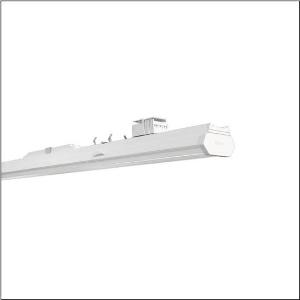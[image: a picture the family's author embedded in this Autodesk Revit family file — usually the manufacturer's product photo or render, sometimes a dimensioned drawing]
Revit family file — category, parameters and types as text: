
# Revit family: licross_r__11_protected_mo_51tp12dn495g3c_6ec9
name_source: partatom
category: Lighting Fixtures
units: mm (PartAtom-declared; Revit-internal decimal feet)

## family parameters
Cut with Voids When Loaded = No
Host = Face
Light Source = No
Part Type = Normal
Room Calculation Point = No
Round Connector Dimension = Use Diameter
Shared = No

## types (1)
- --- (1 x LED, 980 lm, 6.8 W, 4000K)
    Apparent Load = 7 VA
    CIE Flux Codes = 73 92 98 99 100
    Color Rendering = 80
    Color Temperature = 4000K
    Default Elevation = 1800 mm
    Description = Licross® 11 Protected MO, luminaire insert, of sheet steel, galvanised, coil coated, white, length: 1.500mm, width: 90mm, height: 101mm, LED rated luminous flux: 9.980lm, light colour: 840, control gear: DALI 2 (for two DALI lines), with plug, 6-pole, with phase selection, for trunking rail, 14-core, mains connection: 220..240V, AC, 50/60Hz, rated input power: 61W, for trunking rail, 14-core, halogen-free wiring, for emergency light function, converter,control gear: single battery element, battery: LiFePO4, 9Ah, primary light control with lens, of plastic, primary optical cover: cover, of PMMA, light emission: direct distribution, primary light characteristic: symmetric, protection rating (complete): IP64, insulation class (complete): insulation class I (protective earthing), certification: CE, UKCA, protection symbol: D if used in an environment with conductive dust loads with corresponding accessories, impact resistance: IK06, permissible ambient temperature for indoor applications: +5..+35°C, standard: EN 60598-2-22, LABS conformity tested according to VDMA 24364:2018-05, reducing of maximum allowable ambient temperature of 5°C with ceiling mounting, corresponds to IFS (International Featured Standards) requirements for safety and quality in the food industry, packaging unit: 1 piece
    Height = 92 mm
    Lamp = 1 x LED
    Lamp Light Flux = 980 lm
    Lamp Power = 6.8 W
    Lamp count = 1
    Length = 1500 mm
    Luminous efficacy = 144 lm/W
    Manufacturer = Siteco
    ModVariant = No
    Model = 51TP12DN495G3C
    Mounting Place = Ceiling
    Mounting Type = Pendant
    Number of Poles = 1
    OnlyDefault = Yes
    Power Factor = 1
    Product Name = Licross® 11 Protected MO
    Product group = luminaire insert
    ProductGroupID = 901
    Protection Class = Protection class I
    Protection Degree = IP 64
    RLX_Detail_Level = 1
    RLX_Emergency_Light_Flux = 0 lm
    RLX_Emergency_Type = 0
    RLX_Emergency_Type_DB = No
    RlxData = <blob elided: 24777 chars, md5=1fc5c81d>
    Socket = socket
    Standby Power = 0 W
    System Light Flux = 980 lm
    System Power = 7 W
    Type Comments = : emergency light operation: 3 h
    Type Image = l_1256148.jpg
    URL = http://relux.com
    VarID = @adj_059443
    Voltage = 0 V
    Weight = 0.00 kg
    Width = 88 mm

## geometry (parser evidence)
native form markers: Blend x4, Sweep x10
no freeform markers — native parametric forms only
